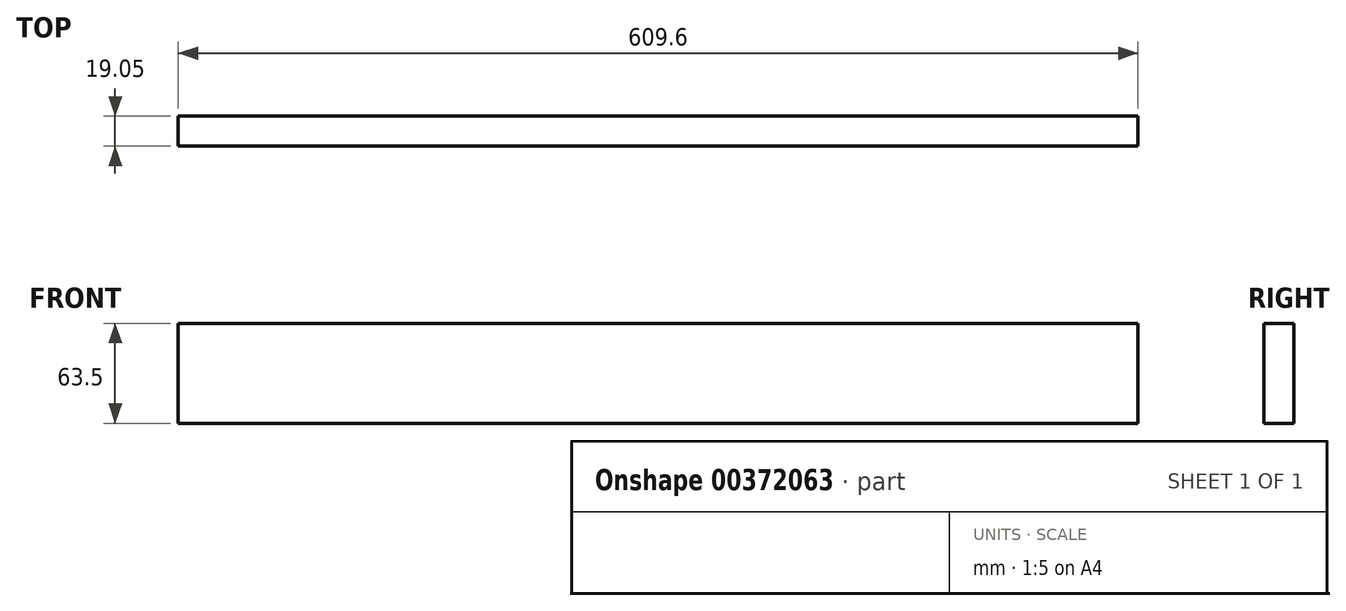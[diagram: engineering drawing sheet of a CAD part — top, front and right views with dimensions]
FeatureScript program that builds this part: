
annotation { "Feature Type Name" : "Feature", "Feature Type Description" : "" }
export const myFeature = defineFeature(function(context is Context, id is Id, definition is map)
    precondition{}
    {
        {
            var Q0;
            Q0=qCreatedBy(makeId("Front.planeOp"),FACE);
            var sketch = newSketch(context, id + "F0", { "sketchPlane" : qUnion([Q0])});
            skLineSegment(sketch, "E0.bottom", {"start": v(0, 0) * mm, "end": v(609.6, 0) * mm});
            skLineSegment(sketch, "E0.top", {"start": v(0, 63.5) * mm, "end": v(609.6, 63.5) * mm});
            skLineSegment(sketch, "E0.left", {"start": v(0, 0) * mm, "end": v(0, 63.5) * mm});
            skLineSegment(sketch, "E0.right", {"start": v(609.6, 0) * mm, "end": v(609.6, 63.5) * mm});
            skSolve(sketch);
        }
        {
            var Q0;
            Q0=makeQuery(id+"F0.imprint","IMPRINT",FACE,{"disambiguationData":[TD([[makeQuery(id+"F0.imprint","IMPRINT",EDGE,{"derivedFrom":sQuery(id+"F0.wireOp",EDGE,"E0.bottom")}),1.0]])]});
            extrude(context, id + "F1", {"entities" : qUnion([Q0]), "oppositeDirection" : true, "depth" : 19.05 * mm});
        }
    });
